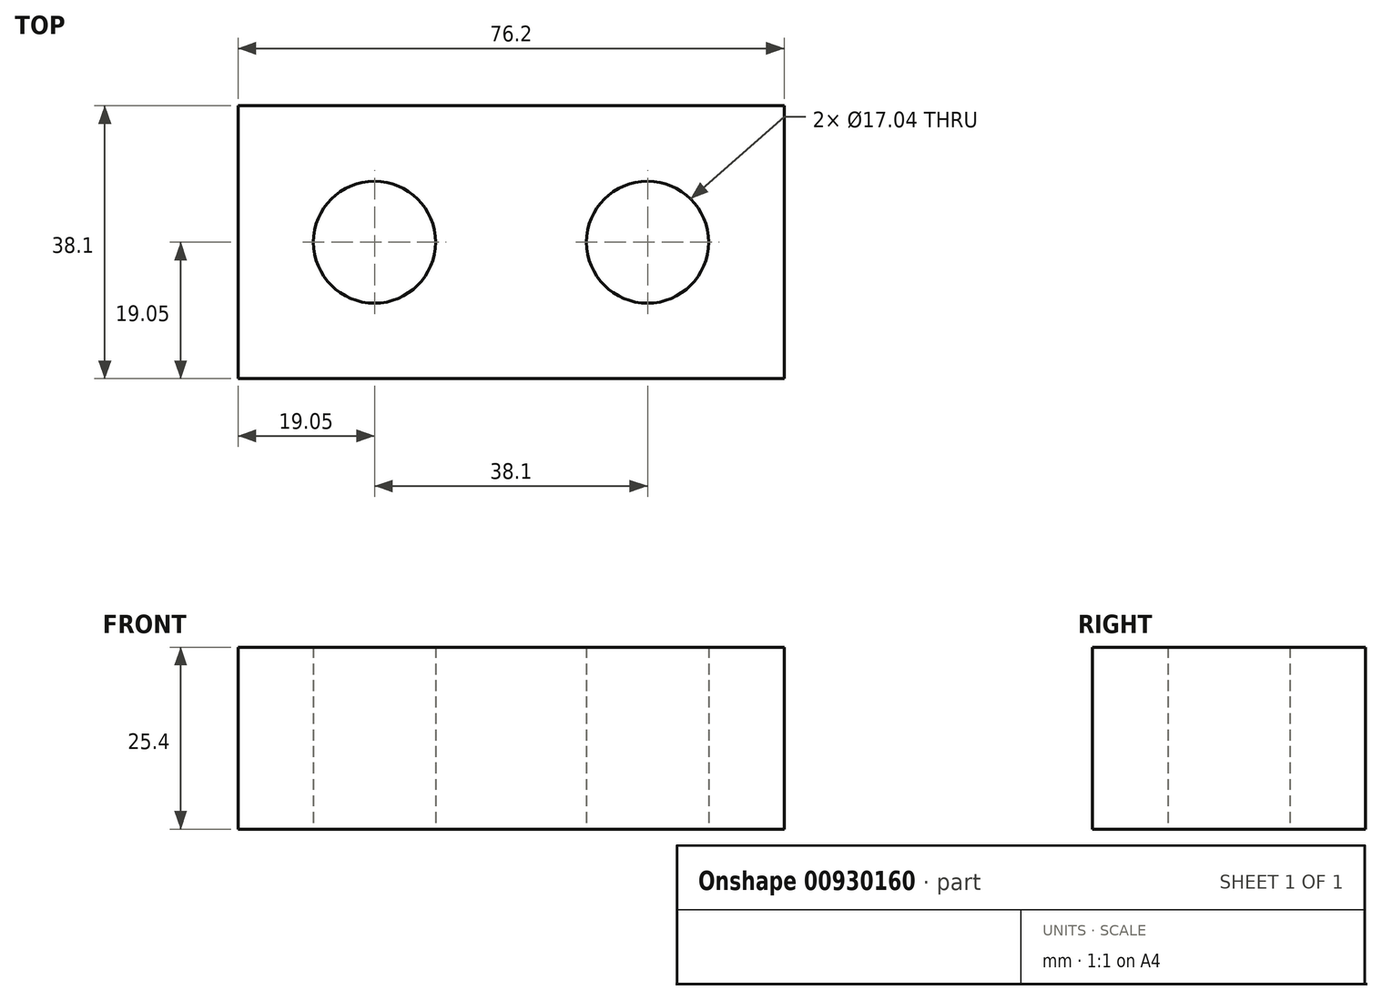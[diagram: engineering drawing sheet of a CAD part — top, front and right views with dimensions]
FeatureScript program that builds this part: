
annotation { "Feature Type Name" : "Feature", "Feature Type Description" : "" }
export const myFeature = defineFeature(function(context is Context, id is Id, definition is map)
    precondition{}
    {
        {
            var Q0;
            Q0=qCreatedBy(makeId("Top.planeOp"),FACE);
            var sketch = newSketch(context, id + "F0", { "sketchPlane" : qUnion([Q0])});
            skLineSegment(sketch, "E0.bottom", {"start": v(0, 0) * mm, "end": v(76.2, 0) * mm});
            skLineSegment(sketch, "E0.top", {"start": v(0, 38.1) * mm, "end": v(76.2, 38.1) * mm});
            skLineSegment(sketch, "E0.left", {"start": v(0, 0) * mm, "end": v(0, 38.1) * mm});
            skLineSegment(sketch, "E0.right", {"start": v(76.2, 0) * mm, "end": v(76.2, 38.1) * mm});
            skCircle(sketch, "E1", {"center": v(19.05, 19.05) * mm, "radius": 8.52 * mm});
            skCircle(sketch, "E2", {"center": v(57.15, 19.05) * mm, "radius": 8.52 * mm});
            skLineSegment(sketch, "E3", {"start": v(0, 19.05) * mm, "end": v(76.2, 19.05) * mm, "construction": true});
            skLineSegment(sketch, "E4", {"start": v(38.1, 38.1) * mm, "end": v(38.1, 0) * mm, "construction": true});
            skLineSegment(sketch, "E5", {"start": v(38.1, 0) * mm, "end": v(19.05, 38.1) * mm, "construction": true});
            skLineSegment(sketch, "E6", {"start": v(0, 38.1) * mm, "end": v(38.1, 38.1) * mm});
            skLineSegment(sketch, "E7", {"start": v(0, 19.05) * mm, "end": v(38.1, 19.05) * mm, "construction": true});
            skLineSegment(sketch, "E8", {"start": v(38.1, 19.05) * mm, "end": v(76.2, 19.05) * mm, "construction": true});
            skLineSegment(sketch, "E9", {"start": v(0, 19.05) * mm, "end": v(10.53, 19.05) * mm, "construction": true});
            skLineSegment(sketch, "E10", {"start": v(10.53, 19.05) * mm, "end": v(48.63, 19.05) * mm, "construction": true});
            skLineSegment(sketch, "E11", {"start": v(65.67, 19.05) * mm, "end": v(76.2, 19.05) * mm, "construction": true});
            skLineSegment(sketch, "E12", {"start": v(19.05, 38.1) * mm, "end": v(19.05, 0) * mm, "construction": true});
            skSolve(sketch);
        }
        {
            var Q0;
            Q0 = qSketchRegion(id + "F0", true);
            extrude(context, id + "F1", {"entities" : qUnion([Q0]), "depth" : 25.4 * mm, "offsetDistance" : 25.4 * mm});
        }
    });
